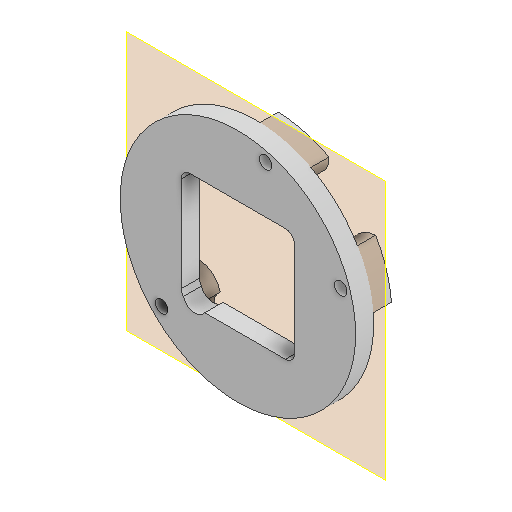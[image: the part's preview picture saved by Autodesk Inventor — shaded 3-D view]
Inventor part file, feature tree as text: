
AUTODESK INVENTOR PART (.ipt)
format: ipt  version: 2022 (Build 260153000, 153)  size: 218,624 bytes
history: native  units: in
note: dims shown in document units (in); Inventor stores cm internally (conversion verified against a paired STEP export)
features: reference x11, other x11, sketch x5, extrude x4, projected_geometry x2, plane x1, hole x1
ambient origin geometry x8: Origin, YZ Plane, XZ Plane, XY Plane, X Axis, Y Axis, Z Axis, Center Point
bodies: Solid1 (feature_tree)
feature tree (35):
  plane  "Work Plane1"
  extrude  "Extrusion1"  Depth=0.9843in
  hole  "Bohrung1"  [1 undecoded]
  extrude  "Extrusion4"  Depth=0.2362in
  extrude  "Extrusion5"  Depth=0.315in
  extrude  "Extrusion6"  Depth=0.315in
  sketch  "Sketch1"  dims[d0=0.1575in d1=0.0in]
  reference  "Reference1"
  reference  "Reference5"
  reference  "Reference6"
  reference  "Reference7"
  sketch  "Skizze4"  dims[d9=0.1102in d10=0.75in d11=0.2559in d12=0.2165in d13=0.5635in d14=1.0in d15=0.8108in d17=0.9843in]
  reference  "Referenz9"
  sketch  "Skizze6"  dims[d18=0.9843in d19=0.0787in]
  projected_geometry  "Projizierte Kontur1"
  sketch  "Skizze7"  dims[d20=0.2362in d21=0.2362in]
  projected_geometry  "Projizierte Kontur2"
  sketch  "Skizze8"  dims[d22=0.1575in d23=0.0in d24=0.315in d25=0.315in d26=0.315in d27=0.1181in d28=0.0in d29=1.5748in d30=0.0197in d31=0.0197in d32=0.0197in d33=0.0197in d34=0.0197in d35=0.0197in d36=0.3937in d37=0.0in]
  reference  "Referenz10"
  reference  "Referenz11"
  reference  "Referenz12"
  reference  "Referenz13"
  reference  "Referenz14"
  reference  "Referenz15"
  other  "<userpath>\Documents\Matchboxscope\INVENTOR\Matchboxscope_v1.iam"
  other  "Matchboxscope_v1.iam"
  other  "Matchboxscope_middle2_v1:1"
  other  "Matchboxscope_middle2_v2:1"
  other  "Anglerfish_lunchbox_m12large_flipped_v0.iam"
  other  "DIN 912 - replaced by DIN EN ISO 4762 M3 x 12:7"
  other  "DIN 912 - replaced by DIN EN ISO 4762 M3 x 12:5"
  other  "DIN 912 - replaced by DIN EN ISO 4762 M3 x 12:1"
  other  "DIN 912 - replaced by DIN EN ISO 4762 M3 x 12:6"
  other  "DIN 912 - replaced by DIN EN ISO 4762 M3 x 12:2"
  other  "DIN 912 - replaced by DIN EN ISO 4762 M3 x 12:4"
note: 1 required parameter value undecoded (feature->parameter linkage not recoverable at this tier; creation-order binding heuristic only, values carry confidence <= 0.55)
